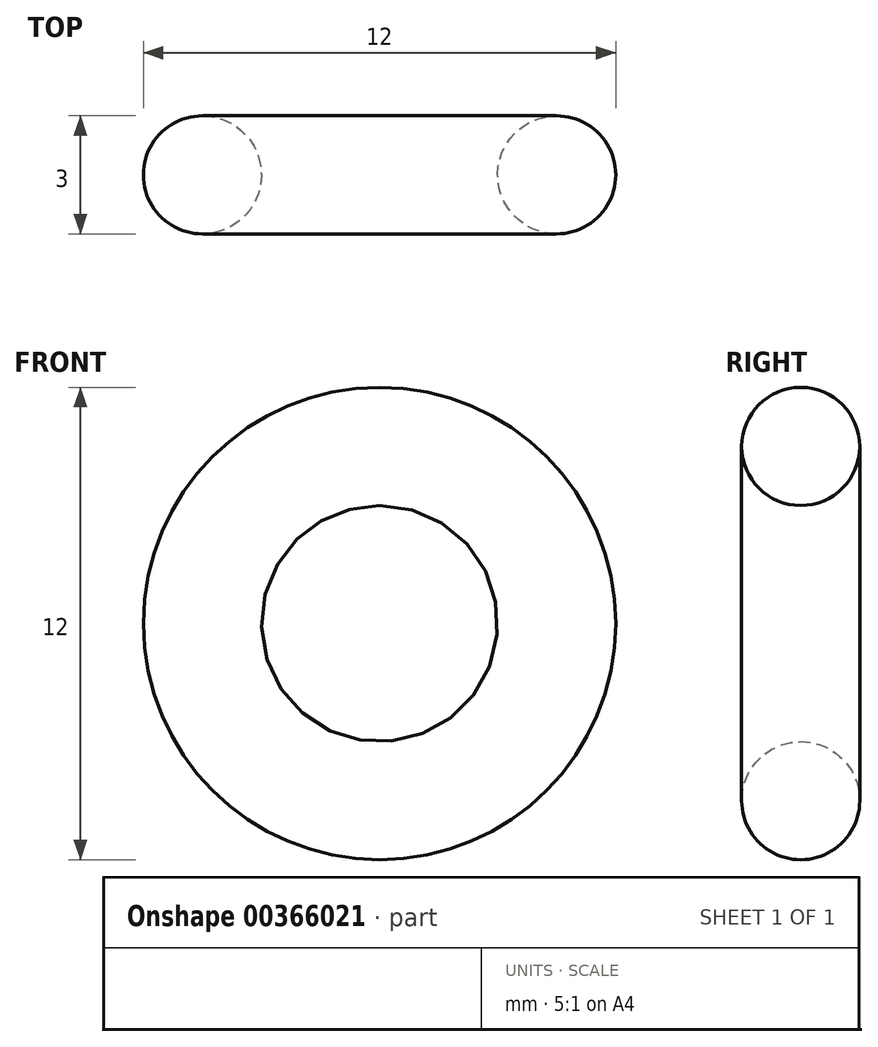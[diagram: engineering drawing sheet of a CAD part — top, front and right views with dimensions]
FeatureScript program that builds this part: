
annotation { "Feature Type Name" : "Feature", "Feature Type Description" : "" }
export const myFeature = defineFeature(function(context is Context, id is Id, definition is map)
    precondition{}
    {
        {
            var Q0;
            Q0=qCreatedBy(makeId("Top.planeOp"),FACE);
            var sketch = newSketch(context, id + "F0", { "sketchPlane" : qUnion([Q0])});
            skCircle(sketch, "E0", {"center": v(4.5, 0) * mm, "radius": 1.5 * mm});
            skSolve(sketch);
        }
        {
            var Q0;
            Q0=qCreatedBy(makeId("Top.planeOp"),FACE);
            var sketch = newSketch(context, id + "F1", { "sketchPlane" : qUnion([Q0])});
            skLineSegment(sketch, "E1", {"start": v(0, 32) * mm, "end": v(0, -27.48) * mm});
            skSolve(sketch);
        }
        {
            var Q0;
            Q0=makeQuery(id+"F0.imprint","IMPRINT",FACE,{"disambiguationData":[TD([[makeQuery(id+"F0.imprint","IMPRINT",EDGE,{"derivedFrom":sQuery(id+"F0.wireOp",EDGE,"E0")}),1.0]])]});
            var Q1;
            Q1=sQuery(id+"F1.wireOp",EDGE,"E1");
            revolve(context, id + "F2", {"entities" : qUnion([Q0]), "axis" : qUnion([Q1]), "revolveType" : RevolveType.FULL});
        }
    });
